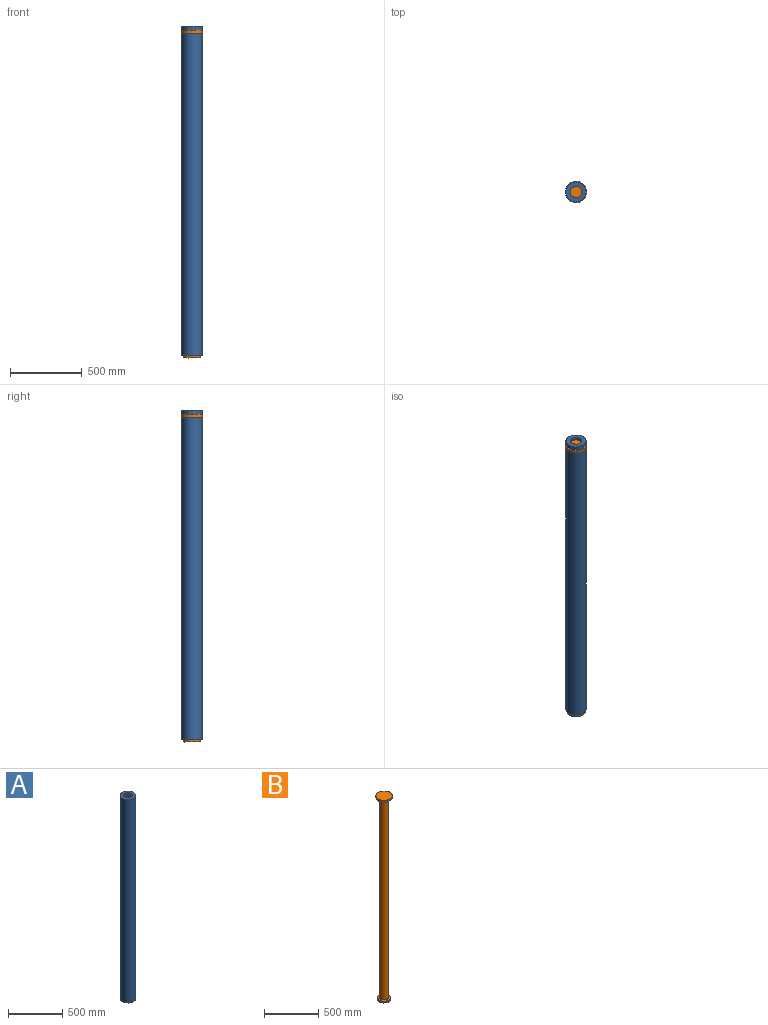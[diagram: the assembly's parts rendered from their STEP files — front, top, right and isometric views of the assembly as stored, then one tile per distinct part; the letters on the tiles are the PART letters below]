
ASSEMBLY  parts=2 mates=1
PART A: 7 faces, bbox 140x140x2300 mm
  f0: plane 120x120mm, normal (0,0,-1), area 6283.2mm2, adj f2,f3
  f1: plane 120x120mm, normal (0,0,1), area 11309.7mm2, adj f2
  f2: cylinder r=60mm len=2235mm, axis (0,0,1), area 842575.1mm2, adj f0,f1
  f3: cylinder r=40mm len=80mm, axis (0,0,1), area 5026.5mm2, adj f0,f5
  f4: cylinder r=70mm len=2300mm, axis (0,0,-1), area 1011592.8mm2, adj f5,f6
  f5: plane 140x140mm, normal (0,0,1), area 10367.3mm2, adj f3,f4
  f6: plane 140x140mm, normal (0,0,-1), area 15393.8mm2, adj f4
PART B: 8 faces, bbox 150x150x2290 mm
  f0: cylinder r=40mm len=2230mm, axis (0,0,-1), area 560460.1mm2, adj f3,f7
  f1: cylinder r=60mm len=120mm, axis (0,0,1), area 7539.8mm2, adj f2,f3
  f2: plane 120x120mm, normal (0,0,-1), area 11309.7mm2, adj f1
  f3: plane 120x120mm, normal (0,0,1), area 6283.2mm2, adj f0,f1
  f4: cylinder r=75mm len=150mm, axis (0,0,-1), area 9424.8mm2, adj f5,f6
  f5: plane 150x150mm, normal (0,0,1), area 17671.5mm2, adj f4
  f6: plane 150x150mm, normal (0,0,-1), area 6361.7mm2, adj f4,f7
  f7: torus R=60mm, axis (0,0,1), area 9330.3mm2, adj f0,f6
PLACE A rot(axis=(-0.03,-0.02,1),0deg) t=(-1132.09,-110.78,-6291.06)mm
PLACE B rot(axis=(-0.03,-0.02,1),0deg) t=(-1132.09,-110.78,-6291.06)mm
MATE slider B.f1 <-> A.f2  axis (0,0,-1) through (-1132.09,-110.78,-6311.06)mm
